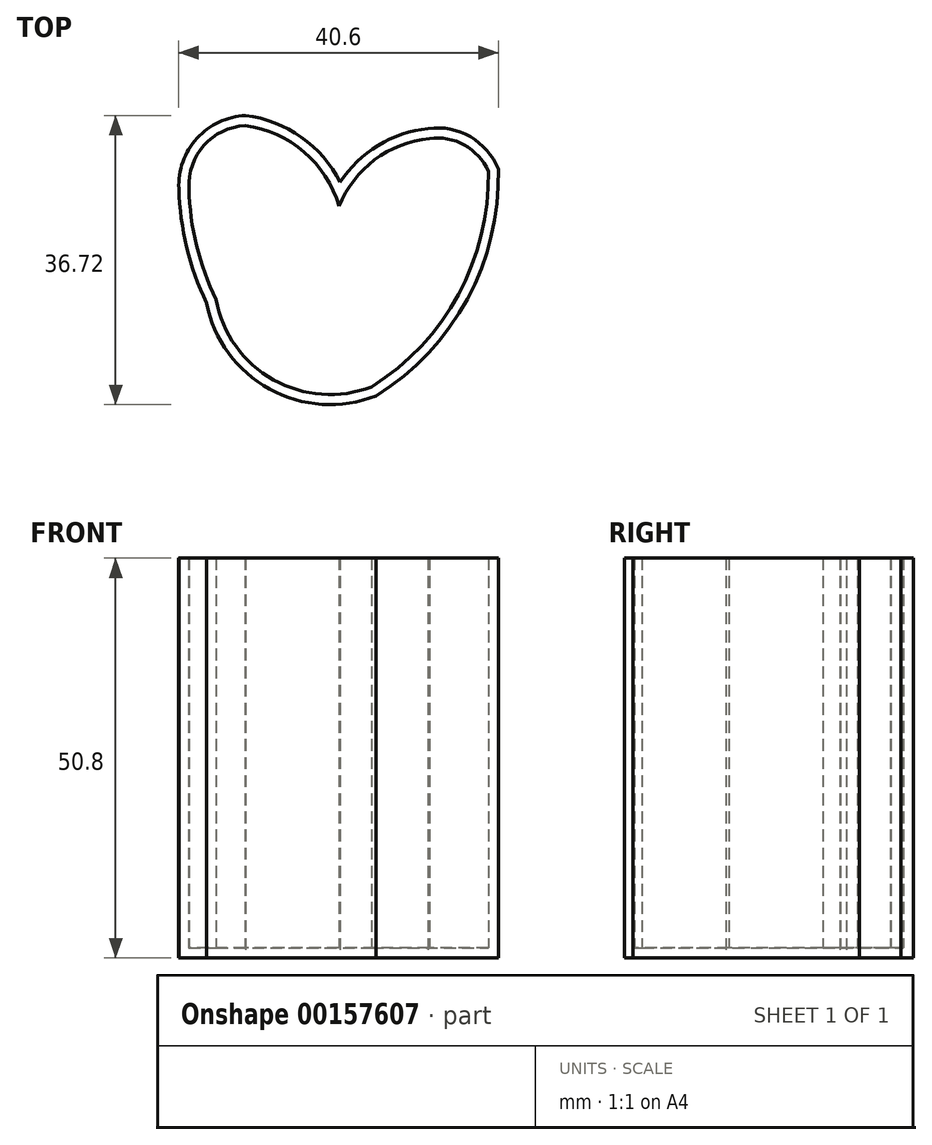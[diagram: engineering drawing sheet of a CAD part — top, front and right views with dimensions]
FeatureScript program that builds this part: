
annotation { "Feature Type Name" : "Feature", "Feature Type Description" : "" }
export const myFeature = defineFeature(function(context is Context, id is Id, definition is map)
    precondition{}
    {
        {
            var Q0;
            Q0=qCreatedBy(makeId("Top.planeOp"),FACE);
            var sketch = newSketch(context, id + "F0", { "sketchPlane" : qUnion([Q0])});
            skArc(sketch, "E0", {"start": v(-57.34, 32.6) * mm, "mid": v(-63.52, 29.71) * mm, "end": v(-65.83, 23.29) * mm});
            skArc(sketch, "E1", {"start": v(-45.34, 24.12) * mm, "mid": v(-50.28, 29.86) * mm, "end": v(-57.34, 32.6) * mm});
            skArc(sketch, "E2", {"start": v(-34.16, 30.95) * mm, "mid": v(-40.52, 28.8) * mm, "end": v(-45.34, 24.12) * mm});
            skArc(sketch, "E3", {"start": v(-25.26, 25.77) * mm, "mid": v(-28.81, 29.9) * mm, "end": v(-34.16, 30.95) * mm});
            skArc(sketch, "E4", {"start": v(-40.78, -3) * mm, "mid": v(-29.17, 9.31) * mm, "end": v(-25.26, 25.77) * mm});
            skArc(sketch, "E5", {"start": v(-62.31, 8.8) * mm, "mid": v(-54.31, -2.15) * mm, "end": v(-40.78, -3) * mm});
            skArc(sketch, "E6", {"start": v(-65.83, 23.29) * mm, "mid": v(-64.83, 15.86) * mm, "end": v(-62.31, 8.8) * mm});
            skSolve(sketch);
        }
        {
            var Q0;
            Q0 = qSketchRegion(id + "F0", true);
            extrude(context, id + "F1", {"entities" : qUnion([Q0]), "depth" : 50.8 * mm});
        }
        {
            var Q0;
            Q0=makeQuery(id+"F1.opExtrude","CAP_FACE",FACE,{"disambiguationData":[OSD([sQuery(id+"F0.wireOp",EDGE,"E0"),sQuery(id+"F0.wireOp",EDGE,"E1"),sQuery(id+"F0.wireOp",EDGE,"E2"),sQuery(id+"F0.wireOp",EDGE,"E3"),sQuery(id+"F0.wireOp",EDGE,"E4"),sQuery(id+"F0.wireOp",EDGE,"E5"),sQuery(id+"F0.wireOp",EDGE,"E6")])],"isStart":false});
            shell(context, id + "F2", {"entities" : qUnion([Q0]), "thickness" : 1.27 * mm});
        }
    });
